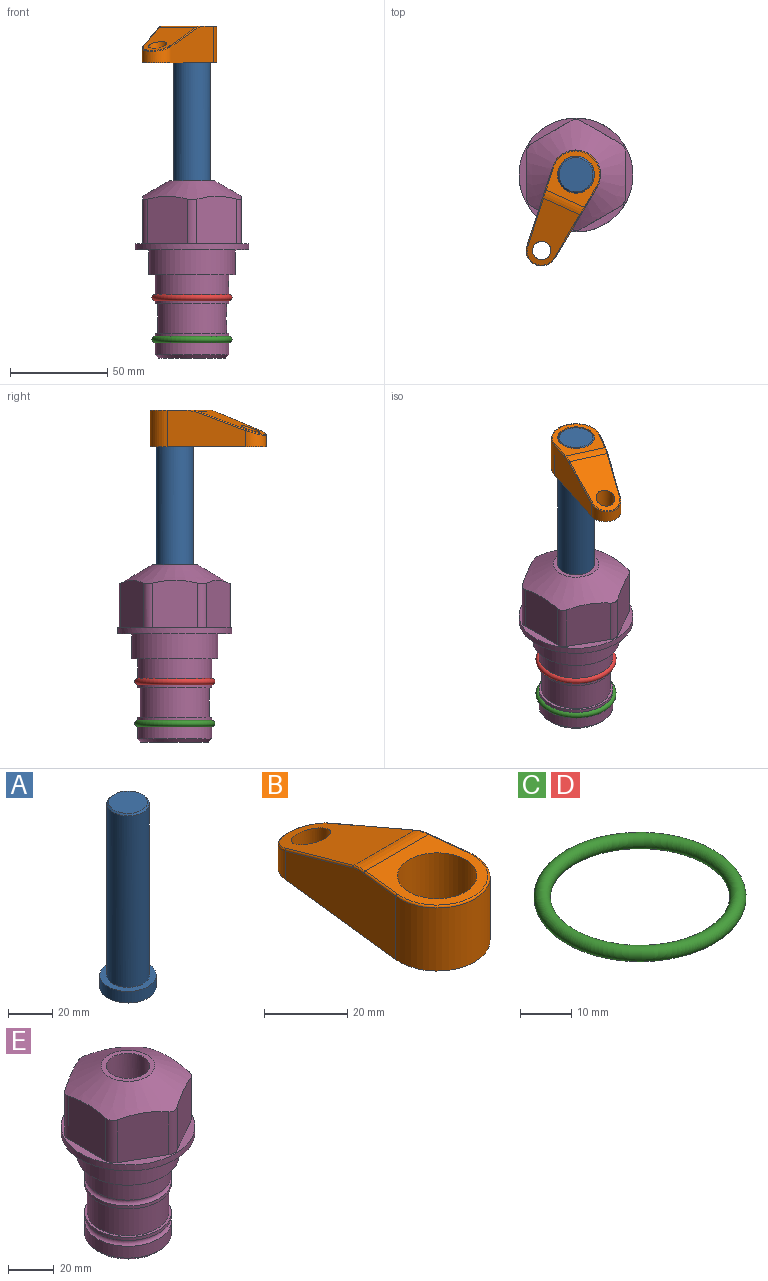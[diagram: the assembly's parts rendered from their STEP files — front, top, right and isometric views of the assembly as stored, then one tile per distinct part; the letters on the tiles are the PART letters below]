
ASSEMBLY  parts=5 mates=3
PART A: 6 faces, bbox 25.4x25.4x101.6 mm
  f0: plane 17.46x17.46mm, normal (0,0,1), area 239.5mm2, adj f5
  f1: plane 25.4x25.4mm, normal (0,0,-1), area 506.7mm2, adj f2
  f2: cylinder r=12.7mm len=25.4mm, axis (0,0,1), area 506.7mm2, adj f1,f3
  f3: plane 25.4x25.4mm, normal (0,0,1), area 221.7mm2, adj f2,f4
  f4: cylinder r=9.53mm len=94.46mm, axis (0,0,1), area 5653mm2, adj f3,f5
  f5: cone r=8.73mm half-angle=45deg, axis (0,0,-1), area 64.4mm2, adj f0,f4
PART B: 44 faces, bbox 27.5x64.5x19.1 mm
  f0: plane 2.3x0.95mm, normal (0,0,-1), area 1mm2, adj f25,f30,f34
  f1: plane 63.5x25.4mm, normal (0,0,-1), area 561.7mm2, adj f2,f3,f4,f5,f6,f7,f19,f20
  f2: cylinder r=12.7mm len=25.4mm, axis (0,0,-1), area 792.2mm2, adj f1,f3,f5,f13
  f3: plane 42.33x18.54mm, normal (0.99,0.11,0), area 647mm2, adj f1,f2,f4,f11,f12,f14
  f4: cylinder r=7.94mm len=15.78mm, axis (0,0,-1), area 158.6mm2, adj f1,f3,f5,f16
  f5: plane 42.33x18.54mm, normal (-0.99,0.11,0), area 647mm2, adj f1,f2,f4,f15,f17,f18
  f6: cylinder r=9.53mm len=19.05mm, axis (0,0,-1), area 1140.1mm2, adj f1,f8
  f7: cylinder r=4.76mm len=10.98mm, axis (0,0,-1), area 276.1mm2, adj f1,f9
  f8: plane 25.83x24.38mm, normal (0,0,1), area 262.2mm2, adj f6,f10,f11,f13,f15
  f9: plane 32.49x20.55mm, normal (0,0.34,0.94), area 489.9mm2, adj f7,f10,f14,f16,f18
  f10: cylinder r=12.7mm len=21.49mm, axis (-1,0,0), area 93.2mm2, adj f8,f9,f12,f17
  f11: cylinder r=0.51mm len=12.34mm, axis (0.11,-0.99,0), area 9.9mm2, adj f3,f8,f12,f13
  f12: bspline ~7.62x1.64mm, area 3.5mm2, adj f3,f10,f11,f14
  f13: torus R=12.19mm, axis (0,0,1), area 33.6mm2, adj f2,f8,f11,f15
  f14: cylinder r=0.51mm len=26.01mm, axis (0.1,-0.93,0.34), area 21.6mm2, adj f3,f9,f12,f16
  f15: cylinder r=0.51mm len=12.34mm, axis (0.11,0.99,0), area 9.9mm2, adj f5,f8,f13,f17
  f16: bspline ~15.78x7.05mm, area 15.7mm2, adj f4,f9,f14,f18
  f17: bspline ~7.62x1.64mm, area 3.5mm2, adj f5,f10,f15,f18
  f18: cylinder r=0.51mm len=26.01mm, axis (0.1,0.93,-0.34), area 21.6mm2, adj f5,f9,f16,f17
  f19: plane 21.6x14.29mm, normal (-0.99,-0.11,0), area 242.6mm2, adj f1,f26,f28,f34,f36,f38
  f20: plane 21.6x14.29mm, normal (0.99,-0.11,0), area 242.6mm2, adj f1,f27,f29,f37,f39,f41
  f21: cylinder r=12.7mm len=14.29mm, axis (0,0,-1), area 173.2mm2, adj f1,f26,f27,f30,f31,f33
  f22: cylinder r=7.94mm len=7.63mm, axis (0,0,-1), area 53.8mm2, adj f1,f28,f29,f42
  f23: plane 2.3x0.95mm, normal (0,0,-1), area 1mm2, adj f25,f33,f37
  f24: plane 17.94x12.32mm, normal (0,-0.34,-0.94), area 191.2mm2, adj f25,f38,f41,f42
  f25: cylinder r=9.53mm len=12.93mm, axis (-1,0,0), area 37.5mm2, adj f0,f23,f24,f31,f36,f39
  f26: cylinder r=1.59mm len=14.29mm, axis (0,0,-1), area 49mm2, adj f1,f19,f21,f32
  f27: cylinder r=1.59mm len=14.29mm, axis (0,0,-1), area 49mm2, adj f1,f20,f21,f35
  f28: cylinder r=1.59mm len=7.28mm, axis (0,0,-1), area 22.1mm2, adj f1,f19,f22,f40
  f29: cylinder r=1.59mm len=7.28mm, axis (0,0,-1), area 22.1mm2, adj f1,f20,f22,f43
  f30: torus R=14.29mm, axis (0,0,1), area 5.8mm2, adj f0,f21,f31,f32
  f31: bspline ~11.06x2.73mm, area 20.8mm2, adj f21,f25,f30,f33
  f32: sphere r=1.59mm, area 5.4mm2, adj f26,f30,f34
  f33: torus R=14.29mm, axis (0,0,1), area 5.8mm2, adj f21,f23,f31,f35
  f34: cylinder r=1.59mm len=1.68mm, axis (-0.11,0.99,0), area 2.4mm2, adj f0,f19,f32,f36
  f35: sphere r=1.59mm, area 5.4mm2, adj f27,f33,f37
  f36: bspline ~5.82x2.33mm, area 7.7mm2, adj f19,f25,f34,f38
  f37: cylinder r=1.59mm len=1.68mm, axis (0.11,0.99,0), area 2.4mm2, adj f20,f23,f35,f39
  f38: cylinder r=1.59mm len=18.33mm, axis (0.1,-0.93,0.34), area 46.7mm2, adj f19,f24,f36,f40
  f39: bspline ~5.82x2.33mm, area 7.7mm2, adj f20,f25,f37,f41
  f40: sphere r=1.59mm, area 3.6mm2, adj f28,f38,f42
  f41: cylinder r=1.59mm len=18.33mm, axis (0.1,0.93,-0.34), area 46.7mm2, adj f20,f24,f39,f43
  f42: bspline ~8.31x1.84mm, area 15.3mm2, adj f22,f24,f40,f43
  f43: sphere r=1.59mm, area 3.6mm2, adj f29,f41,f42
PART C: 1 faces, bbox 44.7x44.7x3.2 mm
  f0: torus R=19.05mm, axis (0,0,1), area 1193.9mm2
PART D: same geometry as C
PART E: 36 faces, bbox 58.7x58.7x91.2 mm
  f0: cylinder r=17.78mm len=35.56mm, axis (0,0,1), area 1670.8mm2, adj f23,f24,f31
  f1: cylinder r=19.05mm len=38.1mm, axis (0,0,1), area 1191.9mm2, adj f26,f27,f30
  f2: plane 58.66x58.66mm, normal (0,0,-1), area 1150.6mm2, adj f3,f28
  f3: cylinder r=29.33mm len=58.66mm, axis (0,0,-1), area 585.1mm2, adj f2,f4
  f4: plane 58.66x58.66mm, normal (0,0,1), area 475.9mm2, adj f3,f5,f6,f7,f8,f9,f10,f11
  f5: plane 24.5x20.32mm, normal (-0.5,0.87,0), area 562.8mm2, adj f4,f15,f16,f17
  f6: plane 24.5x20.32mm, normal (0.5,0.87,0), area 562.8mm2, adj f4,f14,f15,f17
  f7: plane 24.5x23.48mm, normal (1,0,0), area 562.8mm2, adj f4,f13,f14,f17
  f8: plane 24.5x20.32mm, normal (0.5,-0.87,0), area 562.8mm2, adj f4,f12,f13,f17
  f9: plane 24.5x20.32mm, normal (-0.5,-0.87,0), area 562.8mm2, adj f4,f11,f12,f17
  f10: plane 24.5x23.48mm, normal (-1,0,0), area 562.8mm2, adj f4,f11,f16,f17
  f11: cylinder r=5.08mm len=23.01mm, axis (0,0,-1), area 121.2mm2, adj f4,f9,f10,f17
  f12: cylinder r=5.08mm len=23.01mm, axis (0,0,-1), area 121.2mm2, adj f4,f8,f9,f17
  f13: cylinder r=5.08mm len=23.01mm, axis (0,0,-1), area 121.2mm2, adj f4,f7,f8,f17
  f14: cylinder r=5.08mm len=23.01mm, axis (0,0,-1), area 121.2mm2, adj f4,f6,f7,f17
  f15: cylinder r=5.08mm len=23.01mm, axis (0,0,-1), area 121.2mm2, adj f4,f5,f6,f17
  f16: cylinder r=5.08mm len=23.01mm, axis (0,0,-1), area 121.2mm2, adj f4,f5,f10,f17
  f17: cone r=11.73mm half-angle=60deg, axis (0,0,-1), area 2071.8mm2, adj f5,f6,f7,f8,f9,f10,f11,f12
  f18: plane 23.46x23.46mm, normal (0,0,1), area 147.4mm2, adj f17,f35
  f19: plane 34.93x34.93mm, normal (0,0,-1), area 958mm2, adj f29
  f20: cylinder r=19.05mm len=38.1mm, axis (0,0,1), area 760.1mm2, adj f21,f29
  f21: torus R=19.05mm, axis (0,0,1), area 565.3mm2, adj f20,f22
  f22: cylinder r=19.05mm len=38.1mm, axis (0,0,1), area 190mm2, adj f21,f23
  f23: plane 38.1x38.1mm, normal (0,0,1), area 146.9mm2, adj f0,f22
  f24: plane 38.1x38.1mm, normal (0,0,-1), area 146.9mm2, adj f0,f25
  f25: cylinder r=19.05mm len=38.1mm, axis (0,0,1), area 190mm2, adj f24,f26
  f26: torus R=19.05mm, axis (0,0,1), area 565.3mm2, adj f1,f25
  f27: plane 44.45x44.45mm, normal (0,0,-1), area 411.7mm2, adj f1,f28
  f28: cylinder r=22.23mm len=44.45mm, axis (0,0,1), area 1773.5mm2, adj f2,f27
  f29: cone r=19.05mm half-angle=45deg, axis (0,0,1), area 257.5mm2, adj f19,f20
  f30: cylinder r=3.17mm len=6.75mm, axis (-1,0,0), area 128mm2, adj f1,f33
  f31: cylinder r=3.17mm len=6.35mm, axis (-1,0,0), area 102.5mm2, adj f0,f33
  f32: plane 25.4x25.4mm, normal (0,0,1), area 506.7mm2, adj f33
  f33: cylinder r=12.7mm len=66.42mm, axis (0,0,-1), area 5236.2mm2, adj f30,f31,f32,f34
  f34: cone r=9.53mm half-angle=30deg, axis (0,0,-1), area 443.4mm2, adj f33,f35
  f35: cylinder r=9.53mm len=19.05mm, axis (0,0,-1), area 849mm2, adj f18,f34
PLACE A rot(axis=(0,0,-1),114.3deg) t=(0,0,41.67)mm
PLACE B rot(axis=(0,0,1),155.7deg) t=(0,0,96.28)mm
PLACE C t=(0,0,-21.59)mm
PLACE D at identity
PLACE E at identity fixed
MATE fastened C.f0 <-> E.f0  axis (0,0,1) through (0,0,-46.1)mm
MATE cylindrical A.f2 <-> E.f0  axis (0,0,1) through (0,0,67.3)mm
MATE fastened B.f2 <-> A.f2  axis (0,0,1) through (0,0,115.33)mm
